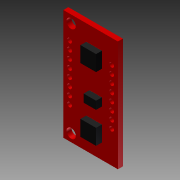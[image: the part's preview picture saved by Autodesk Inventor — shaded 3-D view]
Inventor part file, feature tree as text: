
AUTODESK INVENTOR PART (.ipt)
format: ipt  version: 2012 (Build 160160000, 160)  size: 220,672 bytes
history: native  units: in
note: dims shown in document units (in); Inventor stores cm internally (conversion verified against a paired STEP export)
features: extrude x2, sketch x1, fillet x1
ambient origin geometry x8: Origin, YZ Plane, XZ Plane, XY Plane, X Axis, Y Axis, Z Axis, Center Point
bodies: Solid1 (feature_tree)
feature tree (4):
  sketch  "Sketch1"  dims[d0=3.2283in d1=2.1654in d2=0.689in d3=1.3976in d4=0.4528in d5=0.0984in d6=0.0394in d7=0.3937in d8=1.0825in d9=0.3543in d10=0.3937in d11=0.2362in d12=0.9in d13=0.7569in d14=0.1in d15=0.027in d16=0.3937in d17=0.1in d18=0.02in d19=0.177in d20=0.177in d21=0.1in d22=0.177in d23=0.02in d24=0.1181in d25=0.0591in d26=0.2953in d27=0.0787in d28=0.0591in d29=0.0591in d30=0.0591in d31=0.0591in d32=0.0591in d33=0.0591in d34=0.0591in d35=0.1in d36=0.1in d37=0.1in d38=0.1in d39=0.1in d40=0.1in d41=0.1in d42=0.0591in d43=0.0591in d44=0.0591in d45=0.0591in d46=0.0591in d47=0.0591in d48=0.0591in d49=0.0591in d50=0.1in d51=0.1in d52=0.1in d53=0.1in d54=0.1in d55=0.1in d56=0.1in d57=0.0787in d58=0.2953in d59=0.0787in d60=0.0787in d61=0.0787in d62=0.0787in d63=0.0787in d64=0.0787in d65=0.0787in d66=0.1969in d67=0.1969in d68=0.1969in d69=0.1969in d70=0.0591in d71=0.0591in d72=0.1969in d73=0.1969in d74=0.0591in d75=0.0591in d76=0.0787in d77=0.0787in d78=0.1969in d79=0.1969in d80=0.1in d81=0.1in d82=0.1969in d83=0.1969in d84=0.1575in d85=0.1in d86=0.1969in d87=0.1969in d88=0.1969in d89=0.1969in d90=0.1969in d91=0.1969in d92=0.1969in d93=0.1969in d94=0.1181in d95=0.1181in d96=0.0394in d97=0.0394in d98=0.0394in d99=0.0394in d100=0.0787in d101=0.0in d102=0.005in d103=0.063in d104=0.0in]
  extrude  "Extrusion1"  Depth=0.0787in TaperAngle=0.0deg
  fillet  "Fillet1"  Radius=0.005in
  extrude  "Extrusion2"  Depth=0.063in TaperAngle=0.0deg
